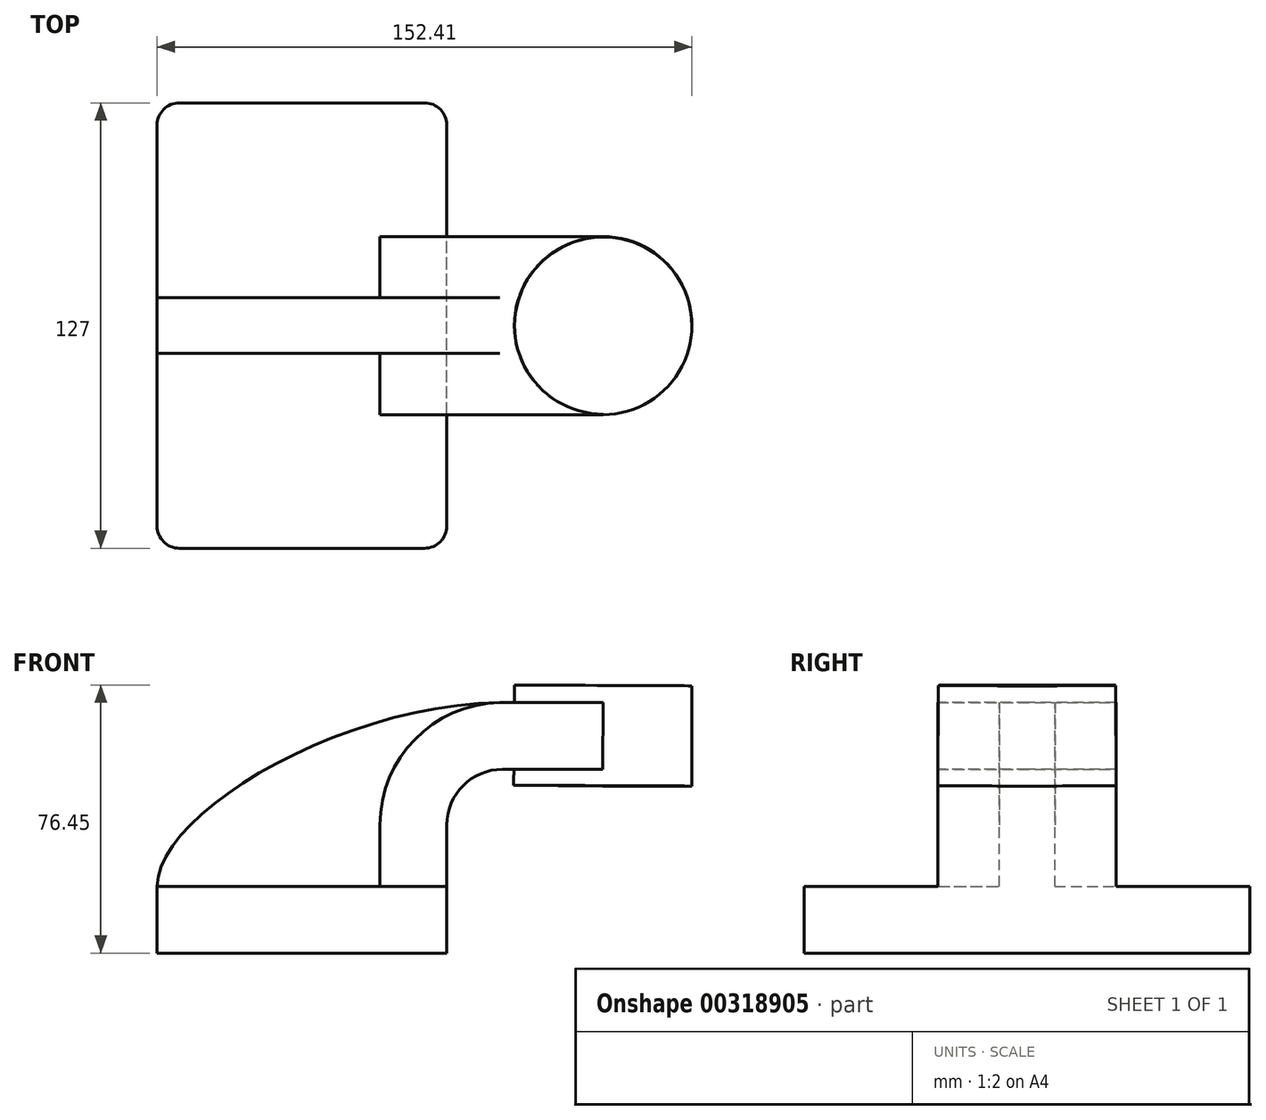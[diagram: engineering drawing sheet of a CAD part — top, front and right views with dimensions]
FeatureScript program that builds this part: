
annotation { "Feature Type Name" : "Feature", "Feature Type Description" : "" }
export const myFeature = defineFeature(function(context is Context, id is Id, definition is map)
    precondition{}
    {
        {
            var Q0;
            Q0=qCreatedBy(makeId("Front.planeOp"),FACE);
            var sketch = newSketch(context, id + "F0", { "sketchPlane" : qUnion([Q0])});
            skLineSegment(sketch, "E0.bottom", {"start": v(41.28, -9.52) * mm, "end": v(-41.28, -9.53) * mm});
            skLineSegment(sketch, "E0.top", {"start": v(41.28, 9.53) * mm, "end": v(-41.28, 9.53) * mm});
            skLineSegment(sketch, "E0.left", {"start": v(41.28, -9.52) * mm, "end": v(41.28, 9.53) * mm});
            skLineSegment(sketch, "E0.right", {"start": v(-41.28, -9.53) * mm, "end": v(-41.28, 9.53) * mm});
            skPoint(sketch, "E0.middle", {"position": v(0, 0) * mm});
            skLineSegment(sketch, "E1.bottom", {"start": v(60.32, 66.68) * mm, "end": v(111.12, 66.68) * mm});
            skLineSegment(sketch, "E1.top", {"start": v(60.33, 38.1) * mm, "end": v(111.12, 38.1) * mm});
            skLineSegment(sketch, "E1.left", {"start": v(60.33, 66.67) * mm, "end": v(60.33, 38.1) * mm});
            skLineSegment(sketch, "E1.right", {"start": v(111.12, 66.68) * mm, "end": v(111.12, 38.1) * mm});
            skPoint(sketch, "E1.middle", {"position": v(85.72, 52.39) * mm});
            skLineSegment(sketch, "E2", {"start": v(41.28, 9.53) * mm, "end": v(41.28, 27) * mm});
            skArc(sketch, "E3", {"start": v(41.27, 27) * mm, "mid": v(45.92, 38.23) * mm, "end": v(57.15, 42.88) * mm});
            skLineSegment(sketch, "E4", {"start": v(57.15, 42.88) * mm, "end": v(85.86, 42.88) * mm});
            skLineSegment(sketch, "E5.0", {"start": v(57.15, 61.93) * mm, "end": v(85.86, 61.93) * mm});
            skArc(sketch, "E5.1", {"start": v(22.23, 27) * mm, "mid": v(32.45, 51.7) * mm, "end": v(57.15, 61.93) * mm});
            skLineSegment(sketch, "E5.2", {"start": v(22.23, 9.53) * mm, "end": v(22.23, 27) * mm});
            skLineSegment(sketch, "E6", {"start": v(85.72, 38.1) * mm, "end": v(85.86, 66.68) * mm});
            skFitSpline(sketch, "E7", {"points": [v(-41.28, 9.53) * mm, v(57.15, 61.93) * mm], "startDerivative": vector(0.15, 62.11) * mm, "endDerivative": vector(139.35, 1.06) * mm});
            skSolve(sketch);
        }
        {
            var Q0;
            Q0=makeQuery(id+"F0.imprint","IMPRINT",FACE,{"disambiguationData":[TD([[makeQuery(id+"F0.imprint","IMPRINT",EDGE,{"derivedFrom":sQuery(id+"F0.wireOp",EDGE,"E0.bottom")}),-1.0]])]});
            extrude(context, id + "F1", {"entities" : qUnion([Q0]), "endBound" : BoundingType.SYMMETRIC, "depth" : 127 * mm});
        }
        {
            var Q0;
            {var subQ0=sQuery(id+"F0.wireOp",EDGE,"E5.0");var subQ1=sQuery(id+"F0.wireOp",EDGE,"E1.left");var subQ2=makeQuery(id+"F0.imprint","INTERSECT",VERTEX,{"derivedFrom":[subQ1,subQ0]});Q0=makeQuery(id+"F0.imprint","IMPRINT",FACE,{"disambiguationData":[TD([[makeQuery(id+"F0.imprint","IMPRINT",EDGE,{"disambiguationData":[TD([[subQ2,-1.0]])],"derivedFrom":subQ1}),1.0]])]});}
            var Q1;
            {var subQ1=sQuery(id+"F0.wireOp",EDGE,"E2");Q1=makeQuery(id+"F0.imprint","IMPRINT",FACE,{"disambiguationData":[TD([[makeQuery(id+"F0.imprint","IMPRINT",EDGE,{"derivedFrom":subQ1}),1.0]])]});}
            extrude(context, id + "F2", {"entities" : qUnion([Q0, Q1]), "operationType" : NewBodyOperationType.ADD, "endBound" : BoundingType.SYMMETRIC, "depth" : 50.8 * mm});
        }
        {
            var Q0;
            {var subQ3=sQuery(id+"F0.wireOp",EDGE,"E5.2");Q0=makeQuery(id+"F0.imprint","IMPRINT",FACE,{"disambiguationData":[TD([[makeQuery(id+"F0.imprint","IMPRINT",EDGE,{"derivedFrom":subQ3}),1.0]])]});}
            extrude(context, id + "F3", {"entities" : qUnion([Q0]), "operationType" : NewBodyOperationType.ADD, "endBound" : BoundingType.SYMMETRIC, "oppositeDirection" : true, "depth" : 15.88 * mm});
        }
        {
            var Q0;
            {var subQ4=sQuery(id+"F0.wireOp",EDGE,"E1.right");Q0=makeQuery(id+"F0.imprint","IMPRINT",FACE,{"disambiguationData":[TD([[makeQuery(id+"F0.imprint","IMPRINT",EDGE,{"derivedFrom":subQ4}),-1.0]])]});}
            var Q1;
            Q1=sQuery(id+"F0.wireOp",EDGE,"E6");
            revolve(context, id + "F4", {"operationType" : NewBodyOperationType.ADD, "entities" : qUnion([Q0]), "axis" : qUnion([Q1]), "revolveType" : RevolveType.FULL});
        }
        {
            var Q0;
            Q0=makeQuery(id+"F1.opExtrude","CAP_EDGE",EDGE,{"disambiguationData":[OSD([sQuery(id+"F0.wireOp",EDGE,"E0.left")])],"isStart":false});
            var Q1;
            Q1=makeQuery(id+"F1.opExtrude","CAP_EDGE",EDGE,{"disambiguationData":[OSD([sQuery(id+"F0.wireOp",EDGE,"E0.right")])],"isStart":false});
            var Q2;
            Q2=makeQuery(id+"F1.opExtrude","CAP_EDGE",EDGE,{"disambiguationData":[OSD([sQuery(id+"F0.wireOp",EDGE,"E0.left")])],"isStart":true});
            var Q3;
            Q3=makeQuery(id+"F1.opExtrude","CAP_EDGE",EDGE,{"disambiguationData":[OSD([sQuery(id+"F0.wireOp",EDGE,"E0.right")])],"isStart":true});
            fillet(context, id + "F5", {"entities" : qUnion([Q0, Q1, Q2, Q3]), "radius" : 6.35 * mm, "tangentPropagation" : true, "allowEdgeOverflow" : false});
        }
    });
